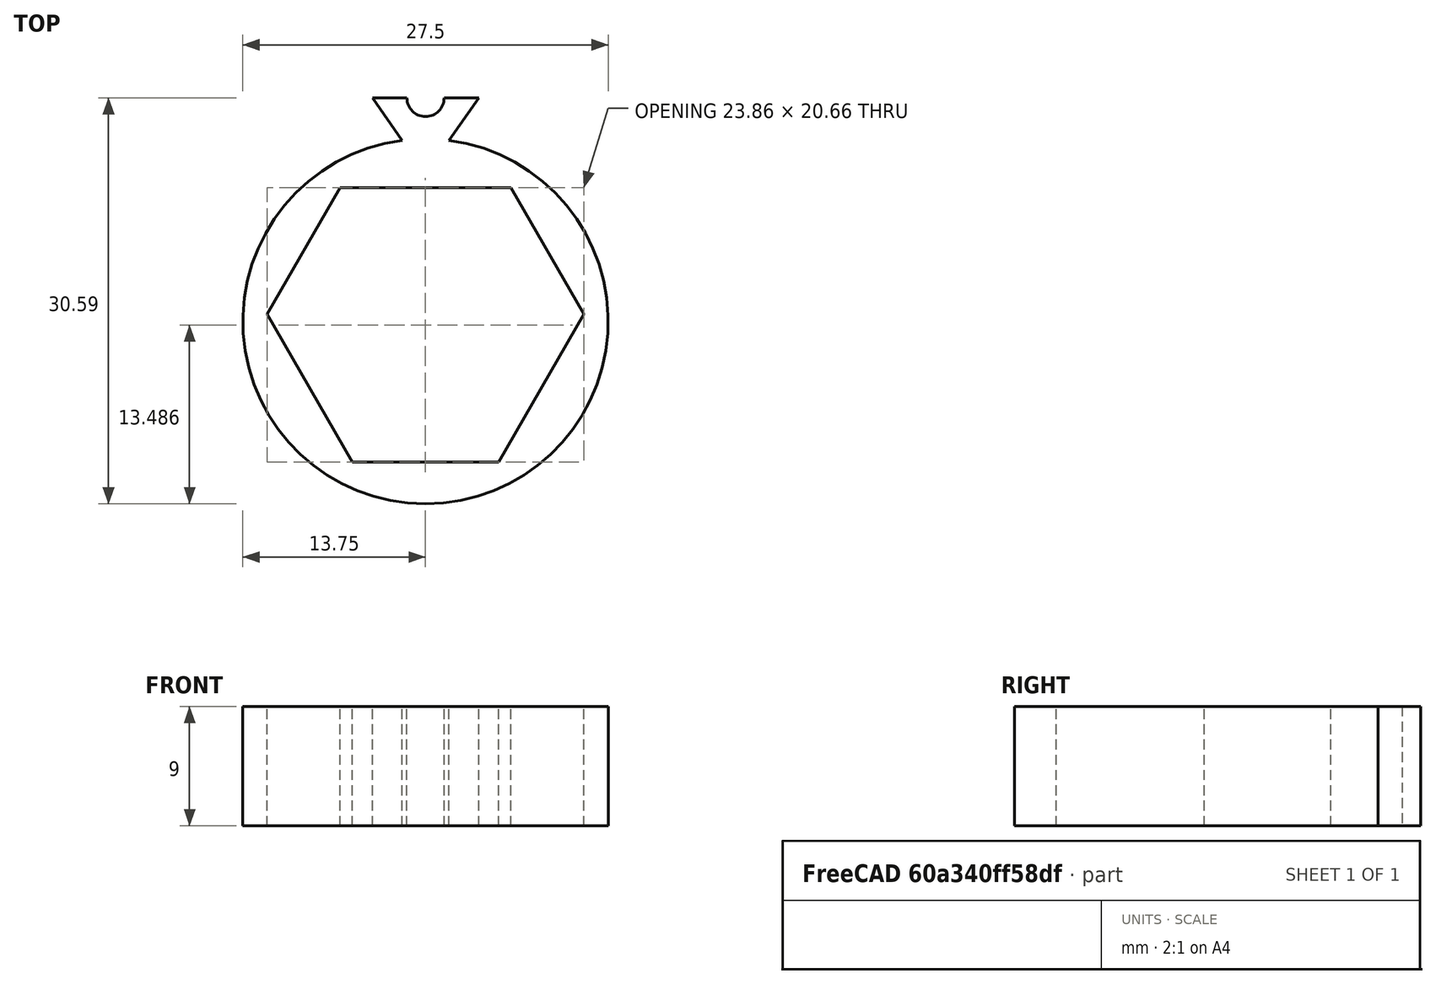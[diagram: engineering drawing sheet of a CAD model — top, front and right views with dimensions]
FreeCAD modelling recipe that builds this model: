
FCSTD DOCUMENT  (FreeCAD 0.19R24291 (Git))
Label: Objective Holder
License: All rights reserved
LicenseURL: http://en.wikipedia.org/wiki/All_rights_reserved
objects: Sketcher::SketchObject×1, PartDesign::Pad×1, PartDesign::Body×1
note: 4 computed .brp shape members not serialized (recipe doc carries the construction recipe); baked Part::Feature solids carry a one-line shape summary decoded from their .brp

FEATURE [Sketcher::SketchObject] Sketch
  FullyConstrained = true
  MapMode = 5
  Support = -> [XY_Plane]
  sketch-geometry (18):
    g0: LineSegment StartX=-1.75 StartY=13.6382 StartZ=0 EndX=-4 EndY=16.8382 EndZ=0
    g1: LineSegment StartX=4 StartY=16.8382 StartZ=0 EndX=1.75 EndY=13.6382 EndZ=0
    g2: LineSegment StartX=-1.75 StartY=13.6382 StartZ=0 EndX=1.75 EndY=13.6382 EndZ=0
    g3: ArcOfCircle CenterX=2e-15 CenterY=16.8382 CenterZ=0 NormalX=0 NormalY=0 NormalZ=1 AngleXU=0 Radius=1.4 StartAngle=3.14159 EndAngle=6.28319
    g4: LineSegment StartX=-1.4 StartY=16.8382 StartZ=0 EndX=-4 EndY=16.8382 EndZ=0
    g5: LineSegment StartX=1.4 StartY=16.8382 StartZ=0 EndX=4 EndY=16.8382 EndZ=0
    g6: ArcOfCircle CenterX=0 CenterY=0 CenterZ=0 NormalX=0 NormalY=0 NormalZ=1 AngleXU=0 Radius=13.75 StartAngle=1.69842 EndAngle=7.72636
    g7: LineSegment StartX=-6.43 StartY=10.0682 StartZ=0 EndX=6.43 EndY=10.0682 EndZ=0
    g8: LineSegment StartX=11.93 StartY=0.541902 StartZ=0 EndX=5.5 EndY=-10.5952 EndZ=0
    g9: LineSegment StartX=-5.5 StartY=-10.5952 StartZ=0 EndX=-11.93 EndY=0.541902 EndZ=0
    g10: LineSegment StartX=0 StartY=-10.5952 StartZ=0 EndX=0 EndY=10.0682 EndZ=0
    g11: GeomPoint X=0 Y=0 Z=0
    g12: LineSegment StartX=-8.715 StartY=-5.02664 StartZ=0 EndX=8.715 EndY=-5.02664 EndZ=0
    g13: LineSegment StartX=0 StartY=10.0682 StartZ=0 EndX=-8.715 EndY=-5.02664 EndZ=0
    g14: LineSegment StartX=0 StartY=10.0682 StartZ=0 EndX=8.715 EndY=-5.02664 EndZ=0
    g15: LineSegment StartX=6.43 StartY=10.0682 StartZ=0 EndX=11.93 EndY=0.541902 EndZ=0
    g16: LineSegment StartX=-6.43 StartY=10.0682 StartZ=0 EndX=-11.93 EndY=0.541902 EndZ=0
    g17: LineSegment StartX=-5.5 StartY=-10.5952 StartZ=0 EndX=5.5 EndY=-10.5952 EndZ=0
  constraints (52):
    c: DistanceX(g0,g1) = 8
    c: DistanceX(g0,g1) = 3.5
    c: DistanceY(g1,g1) = 3.2
    c: Equal(g0,g1)
    c: Coincident(g2,g0)
    c: Coincident(g2,g1)
    c: DistanceX(g0,g3) = 4
    c: Radius(g3) = 1.4
    c: Coincident(g4,g3)
    c: Coincident(g4,g0)
    c: Horizontal(g4)
    c: Coincident(g5,g3)
    c: Coincident(g5,g1)
    c: Horizontal(g5)
    c: DistanceY(g0,g0) = 3.2
    c: Perpendicular(g3,g4)
    c: Coincident(g6,g0)
    c: Coincident(g6,g1)
    c: Diameter(g6) = 27.5
    c: Horizontal(g2)
    c: Coincident(g6,g-1)
    c: Horizontal(g7)
    c: Angle(g9,g7) = 1.0472
    c: Angle(g7,g8) = 1.0472
    c: PointOnObject(g10,g7)
    c: Vertical(g10)
    c: PointOnObject(g12,g8)
    c: PointOnObject(g11,g10)
    c: Coincident(g11,g6)
    c: PointOnObject(g12,g9)
    c: DistanceY(g7,g1) = 3.57
    c: Horizontal(g12)
    c: Equal(g8,g9)
    c: Equal(g9,g7)
    c: Coincident(g13,g10)
    c: Coincident(g14,g10)
    c: DistanceX(g12,g12) = 17.43
    c: Coincident(g15,g7)
    c: Coincident(g15,g8)
    c: Coincident(g16,g7)
    c: Coincident(g16,g9)
    c: Coincident(g17,g9)
    c: Coincident(g17,g8)
    c: Horizontal(g17)
    c: Equal(g17,g16)
    c: Equal(g16,g15)
    c: Coincident(g12,g13)
    c: Coincident(g12,g14)
    c: Equal(g13,g14)
    c: Equal(g14,g12)
    c: PointOnObject(g10,g17)
    c: DistanceX(g17,g17) = 11
FEATURE [PartDesign::Pad] Pad
  Direction = (1,1,1)
  Length = 9
  Length2 = 100
  Profile = -> Sketch
  Type = 0
FEATURE [PartDesign::Body] Body
  Group = -> [Sketch,Pad]
  Origin = -> Origin
  Tip = -> Pad
